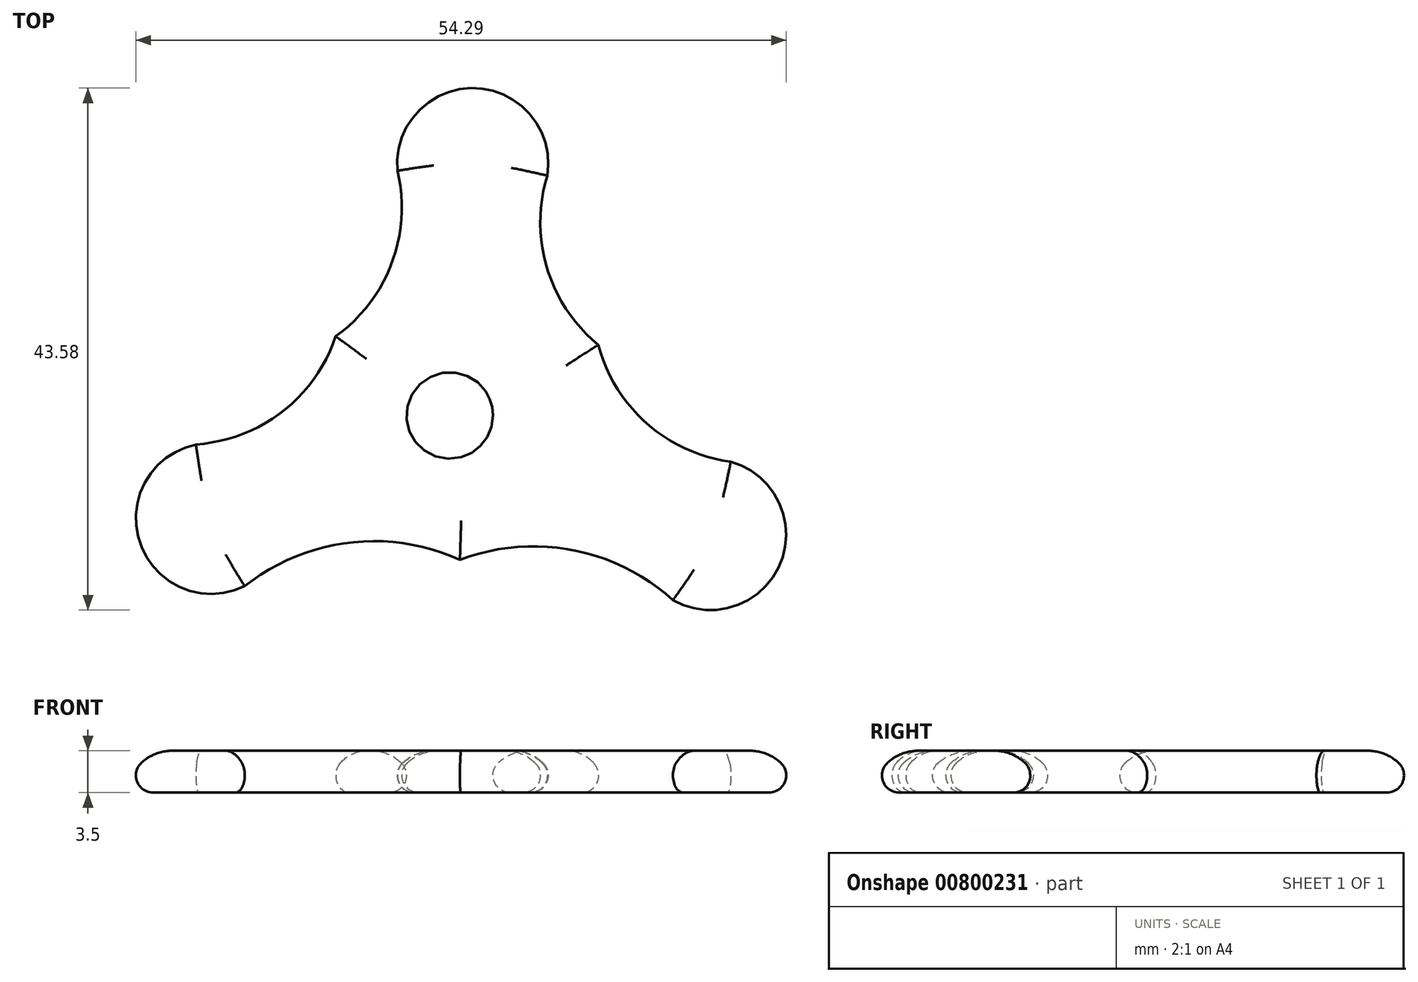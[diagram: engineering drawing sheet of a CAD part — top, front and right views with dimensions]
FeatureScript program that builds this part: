
annotation { "Feature Type Name" : "Feature", "Feature Type Description" : "" }
export const myFeature = defineFeature(function(context is Context, id is Id, definition is map)
    precondition{}
    {
        {
            var Q0;
            Q0=qCreatedBy(makeId("Top.planeOp"),FACE);
            var sketch = newSketch(context, id + "F0", { "sketchPlane" : qUnion([Q0])});
            skLineSegment(sketch, "E0", {"start": v(-74.3, 54.94) * mm, "end": v(74.9, -54.94) * mm});
            skArc(sketch, "E1", {"start": v(-11.57, 8.74) * mm, "mid": v(-7, 14.55) * mm, "end": v(-6.52, 21.94) * mm});
            skLineSegment(sketch, "E2", {"start": v(1.58, 54.94) * mm, "end": v(-1.98, -55.33) * mm});
            skArc(sketch, "E3.MirrorCS", {"start": v(11.72, 7.98) * mm, "mid": v(7.53, 14.08) * mm, "end": v(7.54, 21.48) * mm});
            skLineSegment(sketch, "E4.MirrorCS", {"start": v(77.3, 50.05) * mm, "end": v(-78.66, -49.98) * mm});
            skArc(sketch, "E5", {"start": v(7.54, 21.48) * mm, "mid": v(0.77, 29.76) * mm, "end": v(-6.52, 21.94) * mm});
            skArc(sketch, "E6.MirrorCS", {"start": v(-6.52, 21.94) * mm, "mid": v(0.77, 29.76) * mm, "end": v(7.54, 21.48) * mm});
            skArc(sketch, "E7.MirrorCS", {"start": v(-11.57, 8.74) * mm, "mid": v(-15.76, 2.64) * mm, "end": v(-22.67, 0) * mm});
            skArc(sketch, "E8.MirrorCS", {"start": v(-22.67, 0) * mm, "mid": v(-27.98, -9.28) * mm, "end": v(-18.07, -13.3) * mm});
            skArc(sketch, "E9.MirrorCS", {"start": v(22.24, -1.45) * mm, "mid": v(26.94, -11.05) * mm, "end": v(16.8, -14.42) * mm});
            skArc(sketch, "E10.MirrorCS", {"start": v(11.72, 7.98) * mm, "mid": v(15.52, 1.63) * mm, "end": v(22.24, -1.45) * mm});
            skArc(sketch, "E11", {"start": v(-0.55, -11.27) * mm, "mid": v(-9.6, -9.76) * mm, "end": v(-18.07, -13.3) * mm});
            skArc(sketch, "E12.MirrorCS", {"start": v(-0.55, -11.27) * mm, "mid": v(8.57, -10.34) * mm, "end": v(16.8, -14.42) * mm});
            skSolve(sketch);
        }
        {
            var Q0;
            Q0 = qSketchRegion(id + "F0", true);
            extrude(context, id + "F1", {"entities" : qUnion([Q0]), "depth" : 3.5 * mm, "offsetDistance" : 25 * mm});
        }
        {
            var Q0;
            Q0=makeQuery(id+"F1.opExtrude","CAP_FACE",FACE,{"disambiguationData":[OSD([sQuery(id+"F0.wireOp",EDGE,"E3.MirrorCS"),sQuery(id+"F0.wireOp",EDGE,"E5"),sQuery(id+"F0.wireOp",EDGE,"E8.MirrorCS"),sQuery(id+"F0.wireOp",EDGE,"E1"),sQuery(id+"F0.wireOp",EDGE,"E9.MirrorCS"),sQuery(id+"F0.wireOp",EDGE,"E10.MirrorCS"),sQuery(id+"F0.wireOp",EDGE,"E7.MirrorCS"),sQuery(id+"F0.wireOp",EDGE,"E11"),sQuery(id+"F0.wireOp",EDGE,"E12.MirrorCS")])],"isStart":false});
            var sketch = newSketch(context, id + "F2", { "sketchPlane" : qUnion([Q0])});
            skCircle(sketch, "E13", {"center": v(-1.38, 1.63) * mm, "radius": 2.82 * mm});
            skPoint(sketch, "E13.centerSnap0", {"position": v(15.52, 1.63) * mm});
            skSolve(sketch);
        }
        {
            var Q0;
            Q0 = qSketchRegion(id + "F2", true);
            extrude(context, id + "F3", {"entities" : qUnion([Q0]), "operationType" : NewBodyOperationType.REMOVE, "oppositeDirection" : true, "depth" : 25 * mm, "offsetDistance" : 25 * mm});
        }
        {
            var Q0;
            Q0=makeQuery(id+"F1.opExtrude","CAP_FACE",FACE,{"disambiguationData":[OSD([sQuery(id+"F0.wireOp",EDGE,"E3.MirrorCS"),sQuery(id+"F0.wireOp",EDGE,"E5"),sQuery(id+"F0.wireOp",EDGE,"E8.MirrorCS"),sQuery(id+"F0.wireOp",EDGE,"E1"),sQuery(id+"F0.wireOp",EDGE,"E9.MirrorCS"),sQuery(id+"F0.wireOp",EDGE,"E10.MirrorCS"),sQuery(id+"F0.wireOp",EDGE,"E7.MirrorCS"),sQuery(id+"F0.wireOp",EDGE,"E11"),sQuery(id+"F0.wireOp",EDGE,"E12.MirrorCS")])],"isStart":false});
            fillet(context, id + "F4", {"entities" : qUnion([Q0]), "radius" : 3.86 * mm, "tangentPropagation" : true, "allowEdgeOverflow" : false});
        }
        {
            var Q0;
            Q0=makeQuery(id+"F1.opExtrude","CAP_FACE",FACE,{"disambiguationData":[OSD([sQuery(id+"F0.wireOp",EDGE,"E3.MirrorCS"),sQuery(id+"F0.wireOp",EDGE,"E5"),sQuery(id+"F0.wireOp",EDGE,"E8.MirrorCS"),sQuery(id+"F0.wireOp",EDGE,"E1"),sQuery(id+"F0.wireOp",EDGE,"E9.MirrorCS"),sQuery(id+"F0.wireOp",EDGE,"E10.MirrorCS"),sQuery(id+"F0.wireOp",EDGE,"E7.MirrorCS"),sQuery(id+"F0.wireOp",EDGE,"E11"),sQuery(id+"F0.wireOp",EDGE,"E12.MirrorCS")])],"isStart":true});
            fillet(context, id + "F5", {"entities" : qUnion([Q0]), "radius" : 1.44 * mm, "tangentPropagation" : true, "allowEdgeOverflow" : false});
        }
    });
